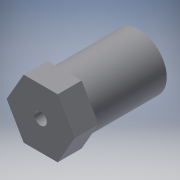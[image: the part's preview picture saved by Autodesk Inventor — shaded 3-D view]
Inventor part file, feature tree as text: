
AUTODESK INVENTOR PART (.ipt)
format: ipt  version: 2016 (Build 200138000, 138)  size: 154,624 bytes
history: native  units: mm
features: sketch x6, extrude x4, hole x2
ambient origin geometry x8: Origin, YZ Plane, XZ Plane, XY Plane, X Axis, Y Axis, Z Axis, Center Point
bodies: Solid1 (feature_tree)
feature tree (12):
  extrude  "Extrusion1"  Depth=4.8mm TaperAngle=0.0deg
  extrude  "Extrusion2"  Depth=3.25mm
  hole  "Hole1"  [1 undecoded]
  hole  "Hole2"  [1 undecoded]
  extrude  "Extrusion8"  Depth=7.621024mm
  extrude  "Extrusion9"  Depth=7.621024mm
  sketch  "Sketch1"  dims[d1=13.65mm d2=4.8mm d3=0.0mm]
  sketch  "Sketch2"  dims[d4=11.0mm d5=3.25mm]
  sketch  "Sketch7"  dims[d7=14.0mm d8=0.0mm d33=3.5mm]
  sketch  "Sketch8"  dims[d34=2.0mm]
  sketch  "Sketch12"  dims[d35=3.2mm d36=6.0mm d37=4.0mm d38=2.0mm d39=90.0deg d40=8.0mm d41=20.594885mm d42=3.0mm]
  sketch  "Sketch14"  dims[d43=2.459mm d44=14.0mm d45=4.0mm d46=2.0mm d47=90.0deg d48=7.0mm d49=20.594885mm d56=2.75mm d64=4.4mm d65=6.0mm d66=0.0mm d67=1.0mm d68=0.0mm d69=7.621024mm]
note: 2 required parameter values undecoded (feature->parameter linkage not recoverable at this tier; creation-order binding heuristic only, values carry confidence <= 0.55)
